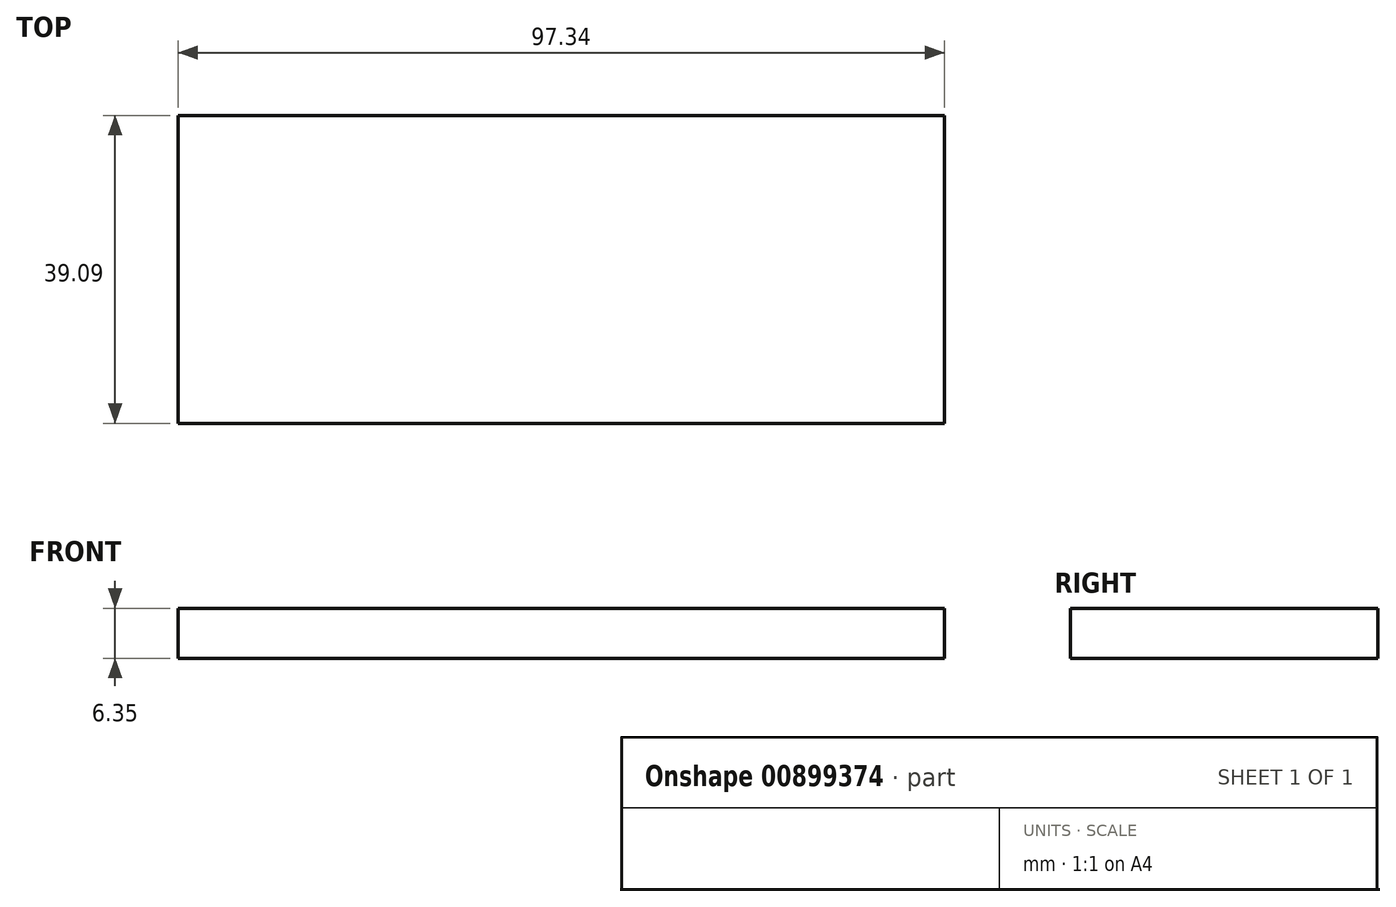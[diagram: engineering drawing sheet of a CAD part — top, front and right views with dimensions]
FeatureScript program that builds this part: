
annotation { "Feature Type Name" : "Feature", "Feature Type Description" : "" }
export const myFeature = defineFeature(function(context is Context, id is Id, definition is map)
    precondition{}
    {
        {
            var Q0;
            Q0=qCreatedBy(makeId("Top.planeOp"),FACE);
            var sketch = newSketch(context, id + "F0", { "sketchPlane" : qUnion([Q0])});
            skLineSegment(sketch, "E0.bottom", {"start": v(-63.3, 20.49) * mm, "end": v(34.04, 20.49) * mm});
            skLineSegment(sketch, "E0.top", {"start": v(-63.3, -18.6) * mm, "end": v(34.04, -18.6) * mm});
            skLineSegment(sketch, "E0.left", {"start": v(-63.3, 20.49) * mm, "end": v(-63.3, -18.6) * mm});
            skLineSegment(sketch, "E0.right", {"start": v(34.04, 20.49) * mm, "end": v(34.04, -18.6) * mm});
            skSolve(sketch);
        }
        {
            var Q0;
            Q0=makeQuery(id+"F0.imprint","IMPRINT",FACE,{"disambiguationData":[TD([[makeQuery(id+"F0.imprint","IMPRINT",EDGE,{"derivedFrom":sQuery(id+"F0.wireOp",EDGE,"E0.bottom")}),-1.0]])]});
            extrude(context, id + "F1", {"entities" : qUnion([Q0]), "depth" : 6.35 * mm, "offsetDistance" : 25.4 * mm});
        }
    });
